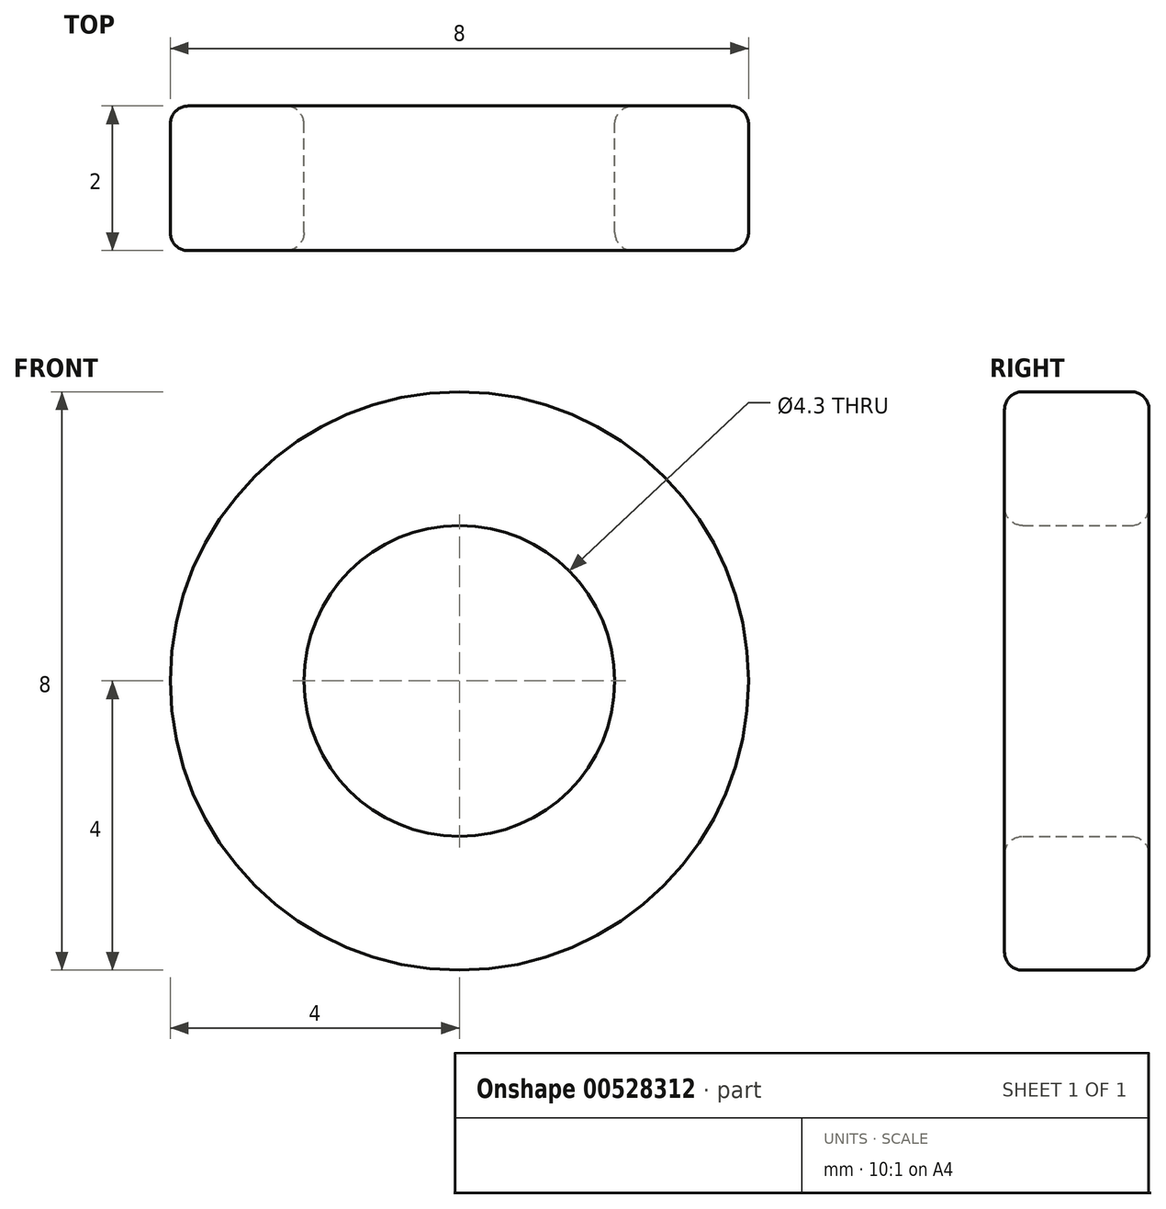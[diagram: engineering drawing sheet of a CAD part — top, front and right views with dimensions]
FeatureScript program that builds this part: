
annotation { "Feature Type Name" : "Feature", "Feature Type Description" : "" }
export const myFeature = defineFeature(function(context is Context, id is Id, definition is map)
    precondition{}
    {
        {
            var Q0;
            Q0=qCreatedBy(makeId("Front.planeOp"),FACE);
            var sketch = newSketch(context, id + "F0", { "sketchPlane" : qUnion([Q0])});
            skCircle(sketch, "E0", {"center": v(0, 0) * mm, "radius": 4 * mm});
            skCircle(sketch, "E1", {"center": v(0, 0) * mm, "radius": 2.15 * mm});
            skSolve(sketch);
        }
        {
            var Q0;
            Q0 = qSketchRegion(id + "F0", true);
            extrude(context, id + "F1", {"entities" : qUnion([Q0]), "depth" : 2 * mm, "offsetDistance" : 25 * mm});
        }
        {
            var Q0;
            Q0=makeQuery(id+"F1.opExtrude","CAP_FACE",FACE,{"disambiguationData":[OSD([sQuery(id+"F0.wireOp",EDGE,"E0"),sQuery(id+"F0.wireOp",EDGE,"E1")])],"isStart":false});
            var Q1;
            Q1=makeQuery(id+"F1.opExtrude","CAP_EDGE",EDGE,{"disambiguationData":[OSD([sQuery(id+"F0.wireOp",EDGE,"E0")])],"isStart":true});
            var Q2;
            Q2=makeQuery(id+"F1.opExtrude","CAP_EDGE",EDGE,{"disambiguationData":[OSD([sQuery(id+"F0.wireOp",EDGE,"E1")])],"isStart":true});
            fillet(context, id + "F2", {"entities" : qUnion([Q0, Q1, Q2]), "radius" : .25 * mm, "tangentPropagation" : true, "allowEdgeOverflow" : false});
        }
    });
